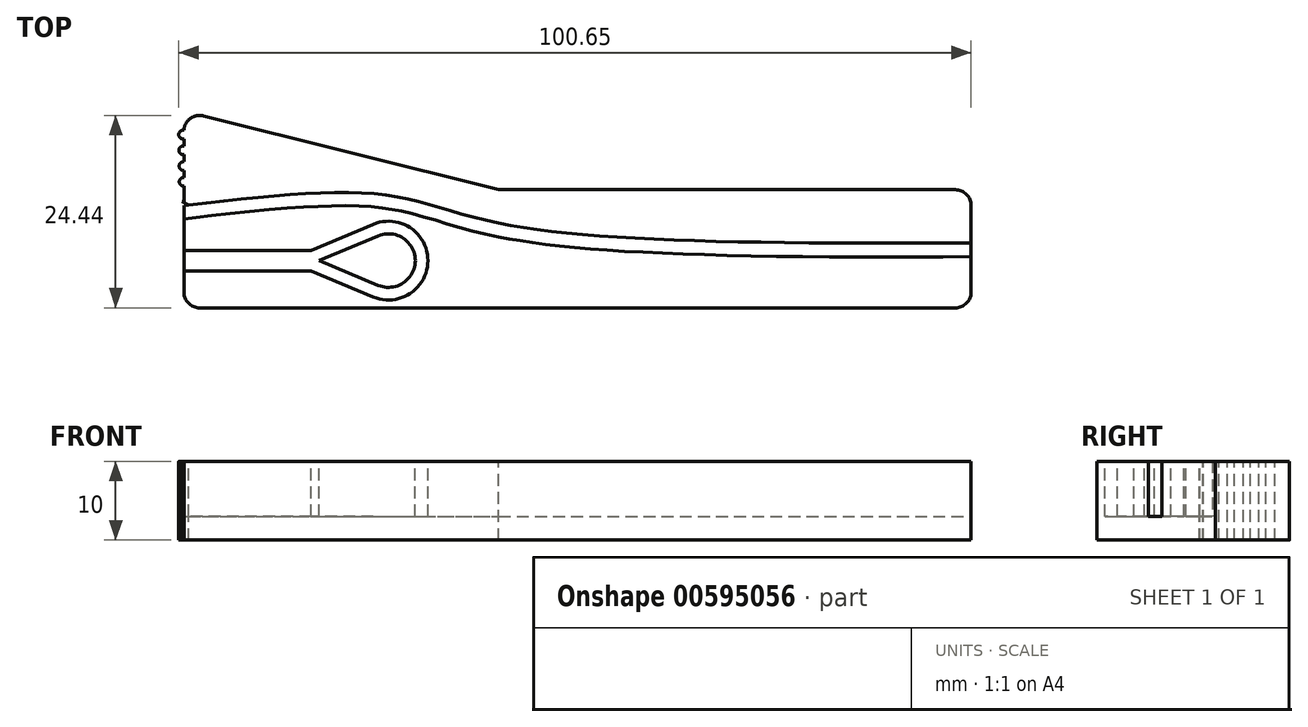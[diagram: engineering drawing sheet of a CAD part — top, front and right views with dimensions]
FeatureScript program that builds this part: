
annotation { "Feature Type Name" : "Feature", "Feature Type Description" : "" }
export const myFeature = defineFeature(function(context is Context, id is Id, definition is map)
    precondition{}
    {
        {
            var Q0;
            Q0=qCreatedBy(makeId("Top.planeOp"),FACE);
            var sketch = newSketch(context, id + "F0", { "sketchPlane" : qUnion([Q0])});
            skLineSegment(sketch, "E0.bottom", {"start": v(0, 7.5) * mm, "end": v(58, 7.5) * mm});
            skLineSegment(sketch, "E0.top", {"start": v(0, -7.5) * mm, "end": v(58, -7.5) * mm});
            skLineSegment(sketch, "E0.left", {"start": v(0, 7.5) * mm, "end": v(0, -7.5) * mm});
            skLineSegment(sketch, "E0.right", {"start": v(60, 5.5) * mm, "end": v(60, -5.5) * mm});
            skLineSegment(sketch, "E1", {"start": v(0, -7.5) * mm, "end": v(-38, -7.5) * mm});
            skLineSegment(sketch, "E2", {"start": v(-40, -5.5) * mm, "end": v(-40, 14.94) * mm});
            skLineSegment(sketch, "E3", {"start": v(-37.51, 16.88) * mm, "end": v(0, 7.5) * mm});
            skPoint(sketch, "E4.visualSharp", {"position": v(-40, 17.5) * mm});
            skArc(sketch, "E4.filletArc", {"start": v(-37.51, 16.88) * mm, "mid": v(-39.23, 16.51) * mm, "end": v(-40, 14.94) * mm});
            skPoint(sketch, "E5.visualSharp", {"position": v(-40, -7.5) * mm});
            skArc(sketch, "E5.filletArc", {"start": v(-40, -5.5) * mm, "mid": v(-39.41, -6.91) * mm, "end": v(-38, -7.5) * mm});
            skPoint(sketch, "E6.visualSharp", {"position": v(60, 7.5) * mm});
            skArc(sketch, "E6.filletArc", {"start": v(60, 5.5) * mm, "mid": v(59.41, 6.91) * mm, "end": v(58, 7.5) * mm});
            skPoint(sketch, "E7.visualSharp", {"position": v(60, -7.5) * mm});
            skArc(sketch, "E7.filletArc", {"start": v(58, -7.5) * mm, "mid": v(59.41, -6.91) * mm, "end": v(60, -5.5) * mm});
            skPoint(sketch, "E8", {"position": v(-14, -1.5) * mm});
            skLineSegment(sketch, "E9.bottom", {"start": v(-18.83, -0.2) * mm, "end": v(-43.6, -0.2) * mm});
            skLineSegment(sketch, "E9.top", {"start": v(-18.83, -2.8) * mm, "end": v(-43.6, -2.8) * mm});
            skLineSegment(sketch, "E9.left", {"start": v(-18.83, -0.2) * mm, "end": v(-18.83, -2.8) * mm});
            skLineSegment(sketch, "E9.right", {"start": v(-43.6, -0.2) * mm, "end": v(-43.6, -2.8) * mm});
            skCircle(sketch, "E10", {"center": v(-14, -1.5) * mm, "radius": 5 * mm});
            skLineSegment(sketch, "E11", {"start": v(-15.93, 3.11) * mm, "end": v(-23.83, -0.2) * mm});
            skLineSegment(sketch, "E12", {"start": v(-15.93, -6.11) * mm, "end": v(-23.83, -2.8) * mm});
            skCircle(sketch, "E13", {"center": v(-14, -1.5) * mm, "radius": 3.4 * mm});
            skCircle(sketch, "E14", {"center": v(-40, 6.51) * mm, "radius": 0.56 * mm});
            skCircle(sketch, "E15.1.0.0", {"center": v(-40.02, 8.51) * mm, "radius": 0.56 * mm});
            skCircle(sketch, "E15.2.0.0", {"center": v(-40.05, 10.5) * mm, "radius": 0.56 * mm});
            skCircle(sketch, "E15.3.0.0", {"center": v(-40.07, 12.5) * mm, "radius": 0.56 * mm});
            skCircle(sketch, "E15.4.0.0", {"center": v(-40.1, 14.5) * mm, "radius": 0.56 * mm});
            skLineSegment(sketch, "E15.direction1", {"start": v(-40, 6.51) * mm, "end": v(-40.02, 8.51) * mm, "construction": true});
            skLineSegment(sketch, "E16", {"start": v(-40.26, 6.02) * mm, "end": v(-39.23, 5.5) * mm});
            skLineSegment(sketch, "E17", {"start": v(-15.32, 1.64) * mm, "end": v(-22.8, -1.5) * mm});
            skLineSegment(sketch, "E18", {"start": v(-22.8, -1.5) * mm, "end": v(-15.32, -4.64) * mm});
            skLineSegment(sketch, "E19.right", {"start": v(100, 0) * mm, "end": v(60, 1.82) * mm});
            skFitSpline(sketch, "E20", {"points": [v(-40.2, 5.5) * mm, v(-14.41, 6.85) * mm, v(0, 3.25) * mm, v(80, 0.91) * mm], "startDerivative": vector(107.73, 12.14) * mm, "endDerivative": vector(235.2, 2.31) * mm});
            skFitSpline(sketch, "E21.0", {"points": [v(-40, 3.81) * mm, v(-37.75, 4.06) * mm, v(-33.39, 4.56) * mm, v(-28.3, 5.06) * mm, v(-24.51, 5.32) * mm, v(-21.82, 5.44) * mm, v(-19.3, 5.47) * mm, v(-16.94, 5.4) * mm, v(-15.15, 5.24) * mm, v(-13.81, 5.05) * mm, v(-12.52, 4.82) * mm, v(-10.97, 4.46) * mm, v(-9.11, 3.94) * mm, v(-7.19, 3.37) * mm, v(-5.13, 2.75) * mm, v(-2.88, 2.14) * mm, v(-0.36, 1.57) * mm, v(2.46, 1.06) * mm, v(6.6, 0.48) * mm, v(12.52, -0.08) * mm, v(20.8, -0.55) * mm, v(33.42, -0.94) * mm, v(52.14, -1.04) * mm, v(70.22, -0.89) * mm, v(80.02, -0.79) * mm]});
            skSolve(sketch);
        }
        {
            var Q0;
            Q0=makeQuery(id+"F0.imprint","IMPRINT",FACE,{"disambiguationData":[TD([[makeQuery(id+"F0.imprint","IMPRINT",EDGE,{"derivedFrom":sQuery(id+"F0.wireOp",EDGE,"E0.left")}),-1.0]])]});
            var Q1;
            Q1=makeQuery(id+"F0.imprint","IMPRINT",FACE,{"disambiguationData":[TD([[makeQuery(id+"F0.imprint","IMPRINT",EDGE,{"derivedFrom":sQuery(id+"F0.wireOp",EDGE,"E0.bottom")}),-1.0]])]});
            var Q2;
            {var subQ5=sQuery(id+"F0.wireOp",EDGE,"E9.left");Q2=makeQuery(id+"F0.imprint","IMPRINT",FACE,{"disambiguationData":[TD([[makeQuery(id+"F0.imprint","IMPRINT",EDGE,{"derivedFrom":subQ5}),-1.0]])]});}
            var Q3;
            Q3=makeQuery(id+"F0.imprint","IMPRINT",FACE,{"disambiguationData":[TD([[makeQuery(id+"F0.imprint","IMPRINT",EDGE,{"derivedFrom":sQuery(id+"F0.wireOp",EDGE,"E13")}),1.0]])]});
            var Q4;
            {var subQ2=sQuery(id+"F0.wireOp",EDGE,"E2");var subQ7=sQuery(id+"F0.wireOp",EDGE,"E9.top");var subQ10=makeQuery(id+"F0.imprint","INTERSECT",VERTEX,{"derivedFrom":[subQ2,subQ7]});Q4=makeQuery(id+"F0.imprint","IMPRINT",FACE,{"disambiguationData":[TD([[makeQuery(id+"F0.imprint","IMPRINT",EDGE,{"disambiguationData":[TD([[subQ10,-1.0]])],"derivedFrom":subQ2}),-1.0]])]});}
            var Q5;
            {var subQ3=sQuery(id+"F0.wireOp",EDGE,"E12");Q5=makeQuery(id+"F0.imprint","IMPRINT",FACE,{"disambiguationData":[TD([[makeQuery(id+"F0.imprint","IMPRINT",EDGE,{"derivedFrom":subQ3}),-1.0]])]});}
            var Q6;
            {var subQ3=sQuery(id+"F0.wireOp",EDGE,"E11");Q6=makeQuery(id+"F0.imprint","IMPRINT",FACE,{"disambiguationData":[TD([[makeQuery(id+"F0.imprint","IMPRINT",EDGE,{"derivedFrom":subQ3}),1.0]])]});}
            var Q7;
            {var subQ1=sQuery(id+"F0.wireOp",EDGE,"E9.left");Q7=makeQuery(id+"F0.imprint","IMPRINT",FACE,{"disambiguationData":[TD([[makeQuery(id+"F0.imprint","IMPRINT",EDGE,{"derivedFrom":subQ1}),1.0]])]});}
            var Q8;
            {var subQ0=sQuery(id+"F0.wireOp",EDGE,"E3");Q8=makeQuery(id+"F0.imprint","IMPRINT",FACE,{"disambiguationData":[TD([[makeQuery(id+"F0.imprint","IMPRINT",EDGE,{"derivedFrom":subQ0}),-1.0]])]});}
            var Q9;
            {var subQ3=sQuery(id+"F0.wireOp",EDGE,"E1");Q9=makeQuery(id+"F0.imprint","IMPRINT",FACE,{"disambiguationData":[TD([[makeQuery(id+"F0.imprint","IMPRINT",EDGE,{"derivedFrom":subQ3}),-1.0]])]});}
            var Q10;
            {var subQ1=sQuery(id+"F0.wireOp",EDGE,"E0.top");Q10=makeQuery(id+"F0.imprint","IMPRINT",FACE,{"disambiguationData":[TD([[makeQuery(id+"F0.imprint","IMPRINT",EDGE,{"derivedFrom":subQ1}),1.0]])]});}
            var Q11;
            {var subQ5=sQuery(id+"F0.wireOp",EDGE,"plTAGgz0-8iha-IrbP-ZtMM-bG7OJEWnxcpc.left");Q11=makeQuery(id+"F0.imprint","IMPRINT",FACE,{"disambiguationData":[TD([[makeQuery(id+"F0.imprint","IMPRINT",EDGE,{"derivedFrom":subQ5}),-1.0]])]});}
            var Q12;
            {var subQ0=sQuery(id+"F0.wireOp",EDGE,"E14");var subQ1=sQuery(id+"F0.wireOp",EDGE,"E2");var subQ3=makeQuery(id+"F0.imprint","INTERSECT",VERTEX,{"derivedFrom":[subQ1,subQ0]});Q12=makeQuery(id+"F0.imprint","IMPRINT",FACE,{"disambiguationData":[TD([[makeQuery(id+"F0.imprint","IMPRINT",EDGE,{"disambiguationData":[TD([[subQ3,1.0]])],"derivedFrom":subQ1}),1.0]])]});}
            var Q13;
            {var subQ0=sQuery(id+"F0.wireOp",EDGE,"E14");var subQ1=sQuery(id+"F0.wireOp",EDGE,"E2");var subQ3=makeQuery(id+"F0.imprint","INTERSECT",VERTEX,{"derivedFrom":[subQ1,subQ0]});Q13=makeQuery(id+"F0.imprint","IMPRINT",FACE,{"disambiguationData":[TD([[makeQuery(id+"F0.imprint","IMPRINT",EDGE,{"disambiguationData":[TD([[subQ3,1.0]])],"derivedFrom":subQ1}),-1.0]])]});}
            var Q14;
            {var subQ0=sQuery(id+"F0.wireOp",EDGE,"E15.1.0.0");var subQ1=sQuery(id+"F0.wireOp",EDGE,"E2");var subQ2=makeQuery(id+"F0.imprint","INTERSECT",VERTEX,{"disambiguationData":[OD(0.0)],"derivedFrom":[subQ1,subQ0]});Q14=makeQuery(id+"F0.imprint","IMPRINT",FACE,{"disambiguationData":[TD([[makeQuery(id+"F0.imprint","IMPRINT",EDGE,{"disambiguationData":[TD([[subQ2,-1.0]])],"derivedFrom":subQ1}),1.0]])]});}
            var Q15;
            {var subQ0=sQuery(id+"F0.wireOp",EDGE,"E15.1.0.0");var subQ1=sQuery(id+"F0.wireOp",EDGE,"E2");var subQ2=makeQuery(id+"F0.imprint","INTERSECT",VERTEX,{"disambiguationData":[OD(0.0)],"derivedFrom":[subQ1,subQ0]});Q15=makeQuery(id+"F0.imprint","IMPRINT",FACE,{"disambiguationData":[TD([[makeQuery(id+"F0.imprint","IMPRINT",EDGE,{"disambiguationData":[TD([[subQ2,-1.0]])],"derivedFrom":subQ1}),-1.0]])]});}
            var Q16;
            {var subQ0=sQuery(id+"F0.wireOp",EDGE,"E15.2.0.0");var subQ1=sQuery(id+"F0.wireOp",EDGE,"E2");var subQ2=makeQuery(id+"F0.imprint","INTERSECT",VERTEX,{"disambiguationData":[OD(0.0)],"derivedFrom":[subQ1,subQ0]});Q16=makeQuery(id+"F0.imprint","IMPRINT",FACE,{"disambiguationData":[TD([[makeQuery(id+"F0.imprint","IMPRINT",EDGE,{"disambiguationData":[TD([[subQ2,-1.0]])],"derivedFrom":subQ1}),1.0]])]});}
            var Q17;
            {var subQ0=sQuery(id+"F0.wireOp",EDGE,"E15.3.0.0");var subQ1=sQuery(id+"F0.wireOp",EDGE,"E2");var subQ2=makeQuery(id+"F0.imprint","INTERSECT",VERTEX,{"disambiguationData":[OD(0.0)],"derivedFrom":[subQ1,subQ0]});Q17=makeQuery(id+"F0.imprint","IMPRINT",FACE,{"disambiguationData":[TD([[makeQuery(id+"F0.imprint","IMPRINT",EDGE,{"disambiguationData":[TD([[subQ2,-1.0]])],"derivedFrom":subQ1}),1.0]])]});}
            var Q18;
            {var subQ0=sQuery(id+"F0.wireOp",EDGE,"E4.filletArc");var subQ1=sQuery(id+"F0.wireOp",EDGE,"E2");var subQ2=makeQuery(id+"F0.imprint","INTERSECT",VERTEX,{"derivedFrom":[subQ1,subQ0]});Q18=makeQuery(id+"F0.imprint","IMPRINT",FACE,{"disambiguationData":[TD([[makeQuery(id+"F0.imprint","IMPRINT",EDGE,{"disambiguationData":[TD([[subQ2,1.0]])],"derivedFrom":subQ1}),1.0]])]});}
            var Q19;
            {var subQ0=sQuery(id+"F0.wireOp",EDGE,"E4.filletArc");var subQ1=sQuery(id+"F0.wireOp",EDGE,"E2");var subQ2=makeQuery(id+"F0.imprint","INTERSECT",VERTEX,{"derivedFrom":[subQ1,subQ0]});Q19=makeQuery(id+"F0.imprint","IMPRINT",FACE,{"disambiguationData":[TD([[makeQuery(id+"F0.imprint","IMPRINT",EDGE,{"disambiguationData":[TD([[subQ2,1.0]])],"derivedFrom":subQ1}),-1.0]])]});}
            var Q20;
            {var subQ0=sQuery(id+"F0.wireOp",EDGE,"E15.3.0.0");var subQ1=sQuery(id+"F0.wireOp",EDGE,"E2");var subQ2=makeQuery(id+"F0.imprint","INTERSECT",VERTEX,{"disambiguationData":[OD(0.0)],"derivedFrom":[subQ1,subQ0]});Q20=makeQuery(id+"F0.imprint","IMPRINT",FACE,{"disambiguationData":[TD([[makeQuery(id+"F0.imprint","IMPRINT",EDGE,{"disambiguationData":[TD([[subQ2,-1.0]])],"derivedFrom":subQ1}),-1.0]])]});}
            var Q21;
            {var subQ0=sQuery(id+"F0.wireOp",EDGE,"E15.2.0.0");var subQ1=sQuery(id+"F0.wireOp",EDGE,"E2");var subQ2=makeQuery(id+"F0.imprint","INTERSECT",VERTEX,{"disambiguationData":[OD(0.0)],"derivedFrom":[subQ1,subQ0]});Q21=makeQuery(id+"F0.imprint","IMPRINT",FACE,{"disambiguationData":[TD([[makeQuery(id+"F0.imprint","IMPRINT",EDGE,{"disambiguationData":[TD([[subQ2,-1.0]])],"derivedFrom":subQ1}),-1.0]])]});}
            var Q22;
            {var subQ0=sQuery(id+"F0.wireOp",EDGE,"plTAGgz0-8iha-IrbP-ZtMM-bG7OJEWnxcpc.bottom");var subQ3=sQuery(id+"F0.wireOp",EDGE,"E16");var subQ5=makeQuery(id+"F0.imprint","INTERSECT",VERTEX,{"derivedFrom":[subQ0,subQ3]});Q22=makeQuery(id+"F0.imprint","IMPRINT",FACE,{"disambiguationData":[TD([[makeQuery(id+"F0.imprint","IMPRINT",EDGE,{"disambiguationData":[TD([[subQ5,1.0]])],"derivedFrom":subQ3}),-1.0]])]});}
            var Q23;
            {var subQ0=sQuery(id+"F0.wireOp",EDGE,"E18");var subQ1=sQuery(id+"F0.wireOp",EDGE,"E17");var subQ2=makeQuery(id+"F0.imprint","INTERSECT",VERTEX,{"derivedFrom":[subQ1,subQ0]});Q23=makeQuery(id+"F0.imprint","IMPRINT",FACE,{"disambiguationData":[TD([[makeQuery(id+"F0.imprint","IMPRINT",EDGE,{"disambiguationData":[TD([[subQ2,1.0]])],"derivedFrom":subQ1}),1.0]])]});}
            var Q24;
            {var subQ1=sQuery(id+"F0.wireOp",EDGE,"E9.top");var subQ3=sQuery(id+"F0.wireOp",EDGE,"E18");var subQ4=makeQuery(id+"F0.imprint","INTERSECT",VERTEX,{"derivedFrom":[subQ1,subQ3]});Q24=makeQuery(id+"F0.imprint","IMPRINT",FACE,{"disambiguationData":[TD([[makeQuery(id+"F0.imprint","IMPRINT",EDGE,{"disambiguationData":[TD([[subQ4,-1.0]])],"derivedFrom":subQ3}),1.0]])]});}
            var Q25;
            {var subQ1=sQuery(id+"F0.wireOp",EDGE,"E9.bottom");var subQ3=sQuery(id+"F0.wireOp",EDGE,"E17");var subQ4=makeQuery(id+"F0.imprint","INTERSECT",VERTEX,{"derivedFrom":[subQ1,subQ3]});Q25=makeQuery(id+"F0.imprint","IMPRINT",FACE,{"disambiguationData":[TD([[makeQuery(id+"F0.imprint","IMPRINT",EDGE,{"disambiguationData":[TD([[subQ4,1.0]])],"derivedFrom":subQ3}),1.0]])]});}
            var Q26;
            {var subQ5=sQuery(id+"F0.wireOp",EDGE,"E10");var subQ8=makeQuery(id+"F0.imprint","INTERSECT",VERTEX,{"derivedFrom":[subQ5,sQuery(id+"F0.wireOp",EDGE,"E11")]});Q26=makeQuery(id+"F0.imprint","IMPRINT",FACE,{"disambiguationData":[TD([[makeQuery(id+"F0.imprint","IMPRINT",EDGE,{"disambiguationData":[TD([[subQ8,-1.0]])],"derivedFrom":subQ5}),1.0]])]});}
            var Q27;
            {var subQ5=sQuery(id+"F0.wireOp",EDGE,"E21.0");var subQ6=sQuery(id+"F0.wireOp",EDGE,"E0.left");var subQ7=makeQuery(id+"F0.imprint","INTERSECT",VERTEX,{"derivedFrom":[subQ6,subQ5]});Q27=makeQuery(id+"F0.imprint","IMPRINT",FACE,{"disambiguationData":[TD([[makeQuery(id+"F0.imprint","IMPRINT",EDGE,{"disambiguationData":[TD([[subQ7,1.0]])],"derivedFrom":subQ6}),1.0]])]});}
            extrude(context, id + "F1", {"entities" : qUnion([Q0, Q1, Q2, Q3, Q4, Q5, Q6, Q7, Q8, Q9, Q10, Q11, Q12, Q13, Q14, Q15, Q16, Q17, Q18, Q19, Q20, Q21, Q22, Q23, Q24, Q25, Q26, Q27]), "oppositeDirection" : true, "depth" : 10 * mm, "offsetDistance" : 25 * mm});
        }
        {
            var Q0;
            {var subQ0=sQuery(id+"F0.wireOp",EDGE,"plTAGgz0-8iha-IrbP-ZtMM-bG7OJEWnxcpc.bottom");var subQ3=sQuery(id+"F0.wireOp",EDGE,"E16");var subQ5=makeQuery(id+"F0.imprint","INTERSECT",VERTEX,{"derivedFrom":[subQ0,subQ3]});Q0=makeQuery(id+"F0.imprint","IMPRINT",FACE,{"disambiguationData":[TD([[makeQuery(id+"F0.imprint","IMPRINT",EDGE,{"disambiguationData":[TD([[subQ5,1.0]])],"derivedFrom":subQ3}),-1.0]])]});}
            var Q1;
            {var subQ2=sQuery(id+"F0.wireOp",EDGE,"E9.top");var subQ5=sQuery(id+"F0.wireOp",EDGE,"E2");var subQ6=makeQuery(id+"F0.imprint","INTERSECT",VERTEX,{"derivedFrom":[subQ5,subQ2]});Q1=makeQuery(id+"F0.imprint","IMPRINT",FACE,{"disambiguationData":[TD([[makeQuery(id+"F0.imprint","IMPRINT",EDGE,{"disambiguationData":[TD([[subQ6,-1.0]])],"derivedFrom":subQ5}),-1.0]])]});}
            var Q2;
            {var subQ5=sQuery(id+"F0.wireOp",EDGE,"plTAGgz0-8iha-IrbP-ZtMM-bG7OJEWnxcpc.left");Q2=makeQuery(id+"F0.imprint","IMPRINT",FACE,{"disambiguationData":[TD([[makeQuery(id+"F0.imprint","IMPRINT",EDGE,{"derivedFrom":subQ5}),-1.0]])]});}
            var Q3;
            {var subQ3=sQuery(id+"F0.wireOp",EDGE,"E12");Q3=makeQuery(id+"F0.imprint","IMPRINT",FACE,{"disambiguationData":[TD([[makeQuery(id+"F0.imprint","IMPRINT",EDGE,{"derivedFrom":subQ3}),-1.0]])]});}
            var Q4;
            {var subQ3=sQuery(id+"F0.wireOp",EDGE,"E11");Q4=makeQuery(id+"F0.imprint","IMPRINT",FACE,{"disambiguationData":[TD([[makeQuery(id+"F0.imprint","IMPRINT",EDGE,{"derivedFrom":subQ3}),1.0]])]});}
            var Q5;
            {var subQ5=sQuery(id+"F0.wireOp",EDGE,"E10");var subQ8=makeQuery(id+"F0.imprint","INTERSECT",VERTEX,{"derivedFrom":[subQ5,sQuery(id+"F0.wireOp",EDGE,"E11")]});Q5=makeQuery(id+"F0.imprint","IMPRINT",FACE,{"disambiguationData":[TD([[makeQuery(id+"F0.imprint","IMPRINT",EDGE,{"disambiguationData":[TD([[subQ8,-1.0]])],"derivedFrom":subQ5}),1.0]])]});}
            var Q6;
            {var subQ5=sQuery(id+"F0.wireOp",EDGE,"E21.0");var subQ6=sQuery(id+"F0.wireOp",EDGE,"E0.left");var subQ7=makeQuery(id+"F0.imprint","INTERSECT",VERTEX,{"derivedFrom":[subQ6,subQ5]});Q6=makeQuery(id+"F0.imprint","IMPRINT",FACE,{"disambiguationData":[TD([[makeQuery(id+"F0.imprint","IMPRINT",EDGE,{"disambiguationData":[TD([[subQ7,1.0]])],"derivedFrom":subQ6}),1.0]])]});}
            var Q7;
            {var subQ0=sQuery(id+"F0.wireOp",EDGE,"E20");var subQ4=sQuery(id+"F0.wireOp",EDGE,"E0.left");var subQ5=makeQuery(id+"F0.imprint","INTERSECT",VERTEX,{"derivedFrom":[subQ4,subQ0]});Q7=makeQuery(id+"F0.imprint","IMPRINT",FACE,{"disambiguationData":[TD([[makeQuery(id+"F0.imprint","IMPRINT",EDGE,{"disambiguationData":[TD([[subQ5,-1.0]])],"derivedFrom":subQ4}),-1.0]])]});}
            extrude(context, id + "F2", {"entities" : qUnion([Q0, Q1, Q2, Q3, Q4, Q5, Q6, Q7]), "operationType" : NewBodyOperationType.REMOVE, "oppositeDirection" : true, "depth" : 7 * mm, "offsetDistance" : 25 * mm});
        }
    });
